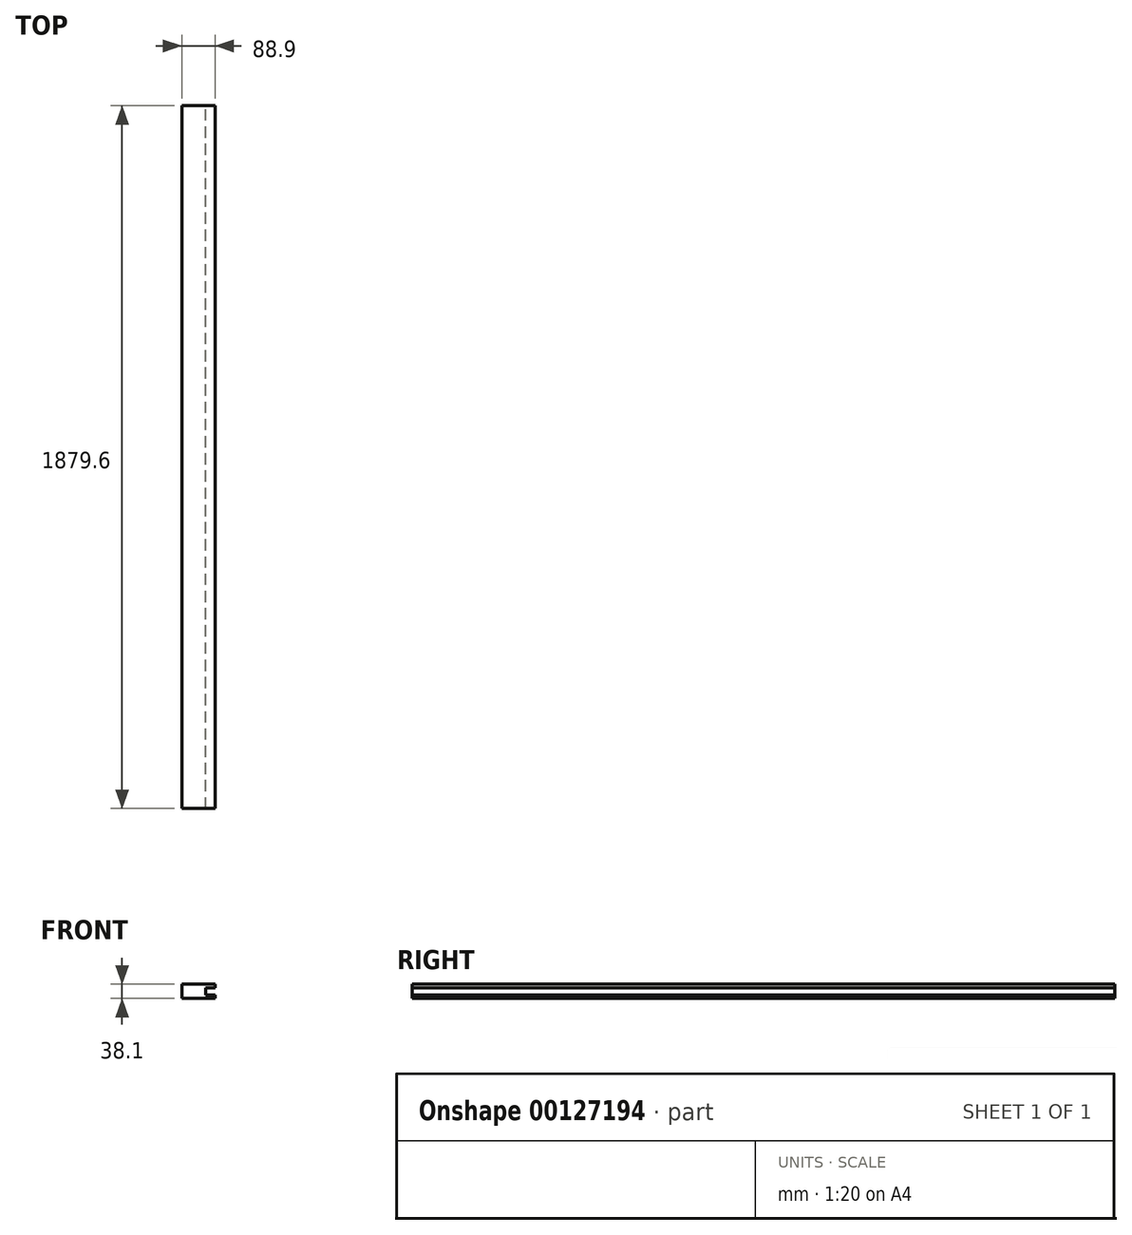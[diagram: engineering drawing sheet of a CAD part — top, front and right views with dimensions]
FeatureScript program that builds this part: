
annotation { "Feature Type Name" : "Feature", "Feature Type Description" : "" }
export const myFeature = defineFeature(function(context is Context, id is Id, definition is map)
    precondition{}
    {
        {
            var Q0;
            Q0=qCreatedBy(makeId("Front.planeOp"),FACE);
            var sketch = newSketch(context, id + "F0", { "sketchPlane" : qUnion([Q0])});
            skLineSegment(sketch, "E0.bottom", {"start": v(44.45, -19.05) * mm, "end": v(-44.45, -19.05) * mm});
            skLineSegment(sketch, "E0.top", {"start": v(44.45, 19.05) * mm, "end": v(-44.45, 19.05) * mm});
            skLineSegment(sketch, "E0.right", {"start": v(-44.45, -19.05) * mm, "end": v(-44.45, 19.05) * mm});
            skPoint(sketch, "E0.middle", {"position": v(0, 0) * mm});
            skLineSegment(sketch, "E1.top", {"start": v(44.45, -9.52) * mm, "end": v(19.05, -9.52) * mm});
            skLineSegment(sketch, "E1.right", {"start": v(19.05, 0) * mm, "end": v(19.05, -9.52) * mm});
            skLineSegment(sketch, "E2.top", {"start": v(44.45, 9.53) * mm, "end": v(19.05, 9.53) * mm});
            skLineSegment(sketch, "E2.right", {"start": v(19.05, 0) * mm, "end": v(19.05, 9.53) * mm});
            skLineSegment(sketch, "E3", {"start": v(44.45, 9.53) * mm, "end": v(44.45, 19.05) * mm});
            skLineSegment(sketch, "E4", {"start": v(44.45, -9.52) * mm, "end": v(44.45, -19.05) * mm});
            skSolve(sketch);
        }
        {
            var Q0;
            Q0=qSketchRegion(id+"F0",true);
            extrude(context, id + "F1", {"entities" : qUnion([Q0]), "depth" : 1879.6 * mm, "offsetDistance" : 25.4 * mm});
        }
    });
